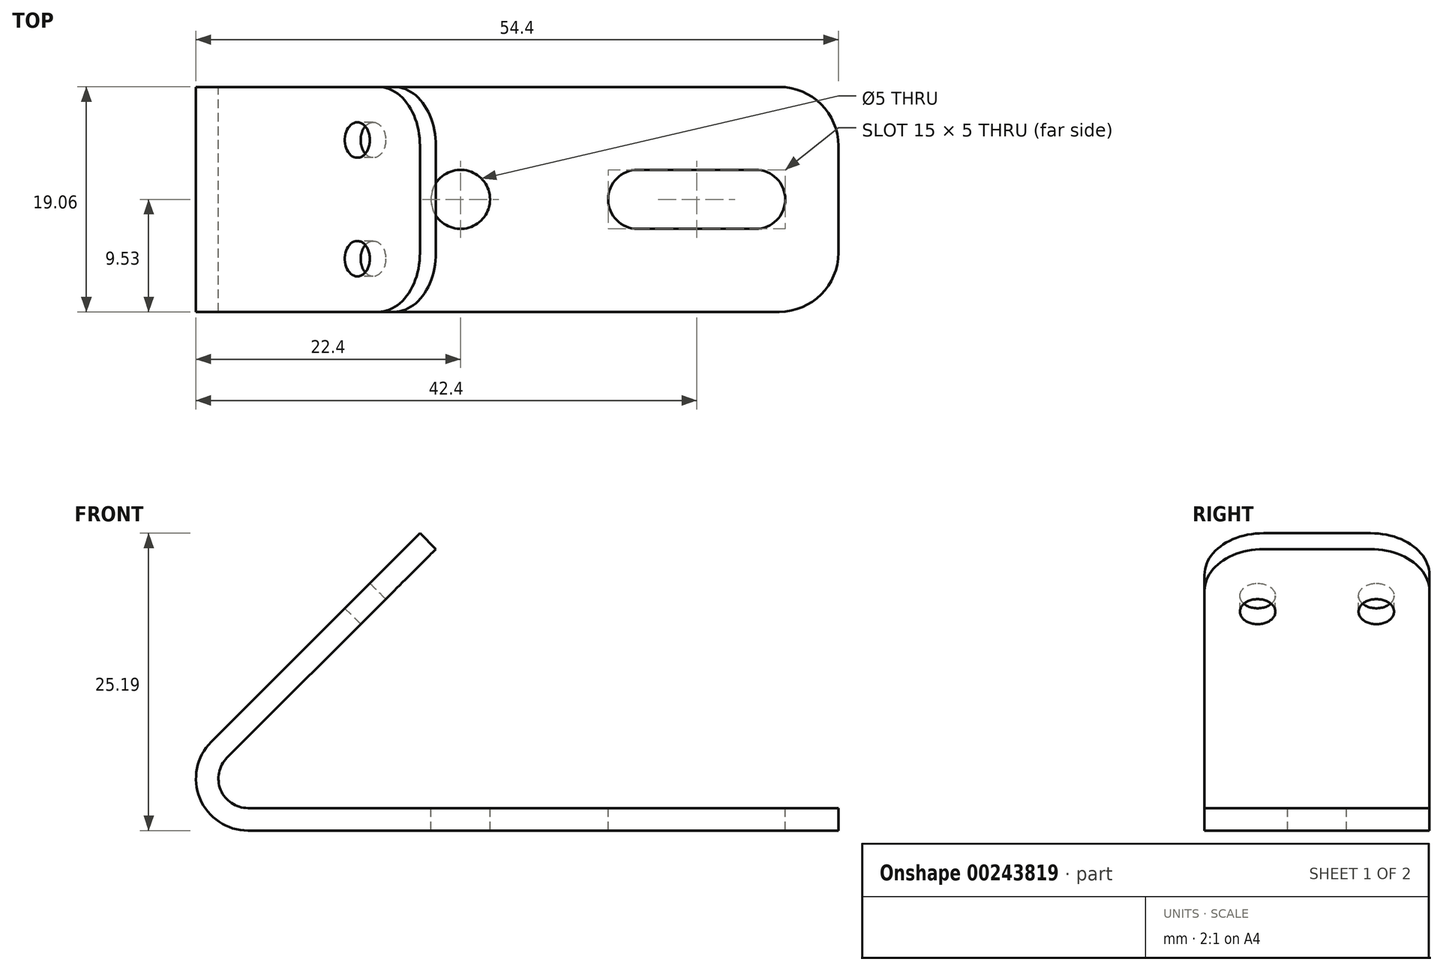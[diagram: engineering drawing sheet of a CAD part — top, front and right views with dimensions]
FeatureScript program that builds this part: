
annotation { "Feature Type Name" : "Feature", "Feature Type Description" : "" }
export const myFeature = defineFeature(function(context is Context, id is Id, definition is map)
    precondition{}
    {
        {
            var Q0;
            Q0=qCreatedBy(makeId("Front.planeOp"),FACE);
            var sketch = newSketch(context, id + "F0", { "sketchPlane" : qUnion([Q0])});
            skLineSegment(sketch, "E0", {"start": v(0, 0) * mm, "end": v(50, 0) * mm});
            skLineSegment(sketch, "E1", {"start": v(50, 0) * mm, "end": v(50, 1.9) * mm});
            skLineSegment(sketch, "E2", {"start": v(50, 1.9) * mm, "end": v(0, 1.9) * mm});
            skLineSegment(sketch, "E3", {"start": v(-3.11, 7.51) * mm, "end": v(14.57, 25.19) * mm});
            skLineSegment(sketch, "E4", {"start": v(14.57, 25.19) * mm, "end": v(15.9, 23.85) * mm});
            skLineSegment(sketch, "E5", {"start": v(15.9, 23.85) * mm, "end": v(-1.77, 6.17) * mm});
            skPoint(sketch, "E6.visualSharp", {"position": v(0, 0) * mm});
            skArc(sketch, "E6.filletArc", {"start": v(-3.11, 7.51) * mm, "mid": v(-4.07, 2.72) * mm, "end": v(0, 0) * mm});
            skArc(sketch, "E7.filletArc", {"start": v(-1.77, 6.17) * mm, "mid": v(-2.3, 3.44) * mm, "end": v(0, 1.9) * mm});
            skSolve(sketch);
        }
        {
            var Q0;
            Q0=makeQuery(id+"F0.imprint","IMPRINT",FACE,{"disambiguationData":[TD([[makeQuery(id+"F0.imprint","IMPRINT",EDGE,{"derivedFrom":sQuery(id+"F0.wireOp",EDGE,"E0")}),1.0]])]});
            extrude(context, id + "F1", {"entities" : qUnion([Q0]), "endBound" : BoundingType.SYMMETRIC, "depth" : 19.05 * mm});
        }
        {
            var Q0;
            Q0=makeQuery(id+"F1.opExtrude","SWEPT_FACE",FACE,{"disambiguationData":[OSD([sQuery(id+"F0.wireOp",EDGE,"E3")])]});
            var sketch = newSketch(context, id + "F2", { "sketchPlane" : qUnion([Q0])});
            skCircle(sketch, "E8", {"center": v(-5.03, 20.61) * mm, "radius": 1.5 * mm});
            skCircle(sketch, "E9", {"center": v(5.03, 20.61) * mm, "radius": 1.5 * mm});
            skSolve(sketch);
        }
        {
            var Q0;
            Q0=sQuery(id+"F2.wireOp",VERTEX,"E8.center");
            var Q1;
            Q1=sQuery(id+"F2.wireOp",VERTEX,"E9.center");
            var Q2;
            Q2=makeQuery(id+"F1.opExtrude","SWEPT_BODY",BODY,{"disambiguationData":[OSD([sQuery(id+"F0.wireOp",EDGE,"E0"),sQuery(id+"F0.wireOp",EDGE,"E1"),sQuery(id+"F0.wireOp",EDGE,"E2"),sQuery(id+"F0.wireOp",EDGE,"E3"),sQuery(id+"F0.wireOp",EDGE,"E4"),sQuery(id+"F0.wireOp",EDGE,"E5"),sQuery(id+"F0.wireOp",EDGE,"E6.filletArc"),sQuery(id+"F0.wireOp",EDGE,"E7.filletArc")])]});
            hole(context, id + "F3", {"style" : HoleStyle.SIMPLE, "endStyle" : HoleEndStyle.BLIND, "holeDiameter" : 3 * mm, "holeDepth" : 12 * mm, "locations" : qUnion([Q0, Q1]), "scope" : qUnion([Q2])});
        }
        {
            var Q0;
            Q0=makeQuery(id+"F1.opExtrude","SWEPT_FACE",FACE,{"disambiguationData":[OSD([sQuery(id+"F0.wireOp",EDGE,"E2")])]});
            var sketch = newSketch(context, id + "F4", { "sketchPlane" : qUnion([Q0])});
            skArc(sketch, "E10", {"start": v(43, -2.5) * mm, "mid": v(45.5, 0) * mm, "end": v(43, 2.5) * mm});
            skArc(sketch, "E11", {"start": v(33, 2.5) * mm, "mid": v(30.5, 0) * mm, "end": v(33, -2.5) * mm});
            skLineSegment(sketch, "E12", {"start": v(33, 2.5) * mm, "end": v(43, 2.5) * mm});
            skLineSegment(sketch, "E13", {"start": v(43, -2.5) * mm, "end": v(33, -2.5) * mm});
            skCircle(sketch, "E14", {"center": v(18, 0) * mm, "radius": 2.5 * mm});
            skSolve(sketch);
        }
        {
            var Q0;
            Q0=makeQuery(id+"F4.imprint","IMPRINT",FACE,{"disambiguationData":[TD([[makeQuery(id+"F4.imprint","IMPRINT",EDGE,{"derivedFrom":sQuery(id+"F4.wireOp",EDGE,"E10")}),1.0]])]});
            var Q1;
            Q1=makeQuery(id+"F4.imprint","IMPRINT",FACE,{"disambiguationData":[TD([[makeQuery(id+"F4.imprint","IMPRINT",EDGE,{"derivedFrom":sQuery(id+"F4.wireOp",EDGE,"E14")}),1.0]])]});
            extrude(context, id + "F5", {"entities" : qUnion([Q0, Q1]), "operationType" : NewBodyOperationType.REMOVE, "oppositeDirection" : true, "depth" : 25 * mm});
        }
        {
            var Q0;
            Q0=makeQuery(id+"F1.opExtrude","CAP_EDGE",EDGE,{"disambiguationData":[OSD([sQuery(id+"F0.wireOp",EDGE,"E1")])],"isStart":false});
            var Q1;
            Q1=makeQuery(id+"F1.opExtrude","CAP_EDGE",EDGE,{"disambiguationData":[OSD([sQuery(id+"F0.wireOp",EDGE,"E1")])],"isStart":true});
            var Q2;
            Q2=makeQuery(id+"F1.opExtrude","CAP_EDGE",EDGE,{"disambiguationData":[OSD([sQuery(id+"F0.wireOp",EDGE,"E4")])],"isStart":false});
            var Q3;
            Q3=makeQuery(id+"F1.opExtrude","CAP_EDGE",EDGE,{"disambiguationData":[OSD([sQuery(id+"F0.wireOp",EDGE,"E4")])],"isStart":true});
            fillet(context, id + "F6", {"entities" : qUnion([Q0, Q1, Q2, Q3]), "radius" : 5 * mm, "tangentPropagation" : true, "allowEdgeOverflow" : false});
        }
    });
